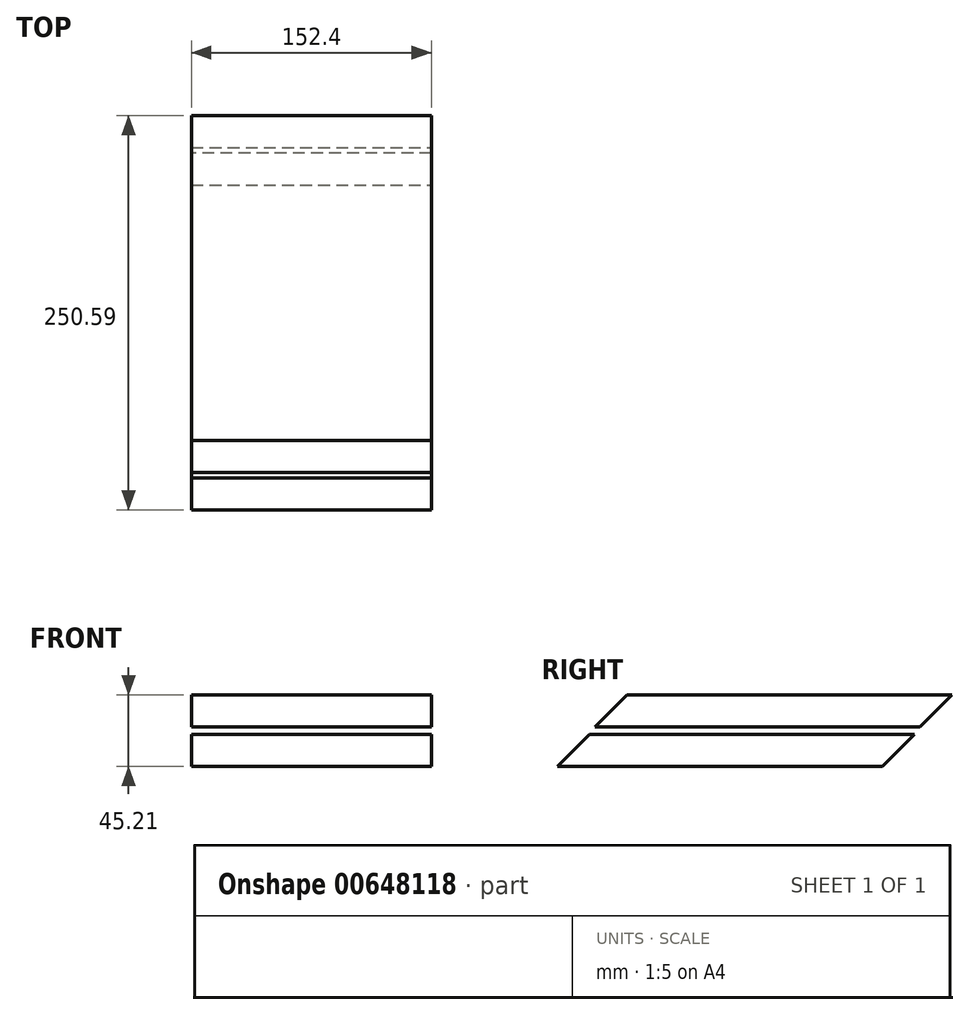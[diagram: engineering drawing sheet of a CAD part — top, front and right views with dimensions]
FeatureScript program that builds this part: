
annotation { "Feature Type Name" : "Feature", "Feature Type Description" : "" }
export const myFeature = defineFeature(function(context is Context, id is Id, definition is map)
    precondition{}
    {
        {
            var Q0;
            Q0=qCreatedBy(makeId("Top.planeOp"),FACE);
            var sketch = newSketch(context, id + "F0", { "sketchPlane" : qUnion([Q0])});
            skLineSegment(sketch, "E0.bottom", {"start": v(-76.34, -75.7) * mm, "end": v(76.06, -75.7) * mm});
            skLineSegment(sketch, "E0.top", {"start": v(-76.34, 161.17) * mm, "end": v(76.06, 161.17) * mm});
            skLineSegment(sketch, "E0.left", {"start": v(-76.34, -75.7) * mm, "end": v(-76.34, 161.17) * mm});
            skLineSegment(sketch, "E0.right", {"start": v(76.06, -75.7) * mm, "end": v(76.06, 161.17) * mm});
            skSolve(sketch);
        }
        {
            var Q0;
            Q0 = qSketchRegion(id + "F0", true);
            extrude(context, id + "F1", {"entities" : qUnion([Q0]), "depth" : 20.32 * mm, "offsetDistance" : 25.4 * mm});
        }
        {
            var Q0;
            Q0=makeQuery(id+"F1.opExtrude","CAP_EDGE",EDGE,{"disambiguationData":[OSD([sQuery(id+"F0.wireOp",EDGE,"E0.bottom")])],"isStart":false});
            chamfer(context, id + "F2", {"entities" : qUnion([Q0]), "width" : 25.4 * mm, "tangentPropagation" : true});
        }
        {
            var Q0;
            Q0=makeQuery(id+"F1.opExtrude","CAP_EDGE",EDGE,{"disambiguationData":[OSD([sQuery(id+"F0.wireOp",EDGE,"E0.top")])],"isStart":true});
            chamfer(context, id + "F3", {"entities" : qUnion([Q0]), "width" : 25.4 * mm, "tangentPropagation" : true});
        }
        {
            var Q0;
            Q0=makeQuery(id+"F1.opExtrude","SWEPT_BODY",BODY,{"disambiguationData":[OSD([sQuery(id+"F0.wireOp",EDGE,"E0.bottom"),sQuery(id+"F0.wireOp",EDGE,"E0.top"),sQuery(id+"F0.wireOp",EDGE,"E0.left"),sQuery(id+"F0.wireOp",EDGE,"E0.right")])]});
            transform(context, id + "F4", {"entities" : qUnion([Q0]), "transformType" : TransformType.TRANSLATION_3D, "dx" : 0 * mm, "dy" : 23.88 * mm, "dz" : 24.9 * mm, "makeCopy" : true});
        }
        {
            var Q0;
            Q0=sQuery(id+"F0.wireOp",EDGE,"E0.right");
            extrude(context, id + "F5", {"bodyType" : ToolBodyType.SURFACE, "surfaceEntities" : qUnion([Q0]), "depth" : 7.62 * mm, "offsetDistance" : 25.4 * mm});
        }
    });
